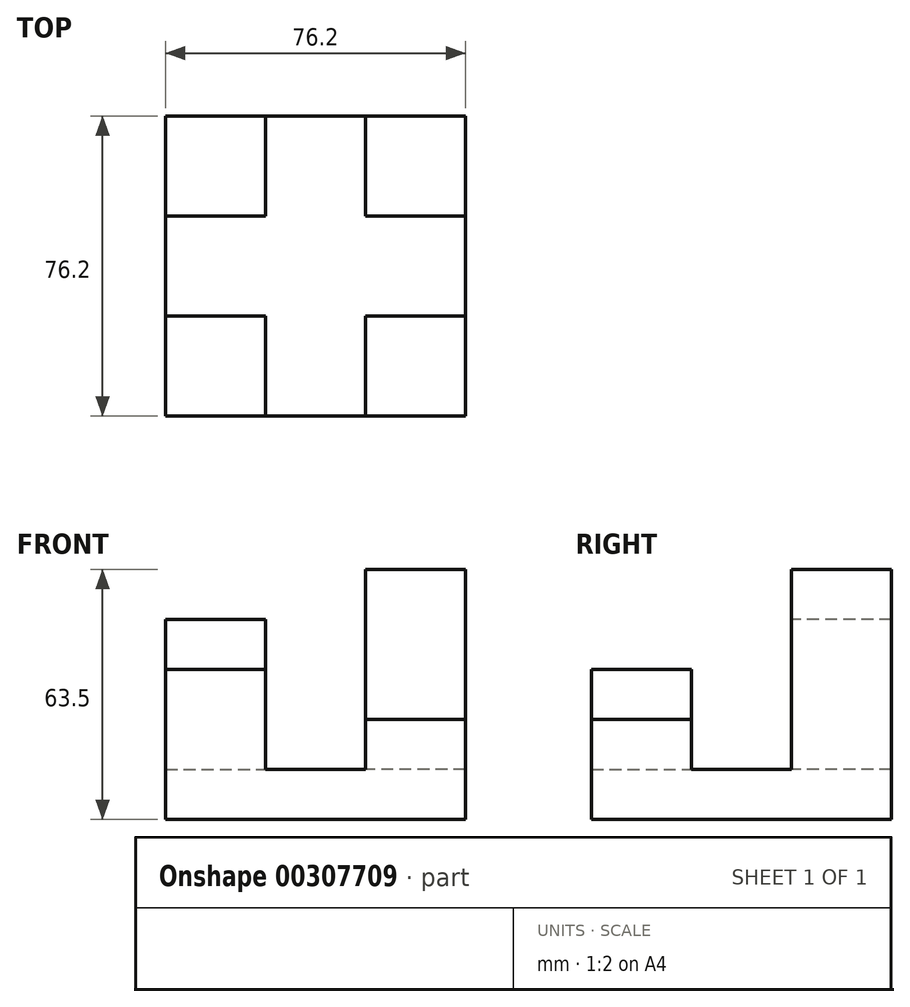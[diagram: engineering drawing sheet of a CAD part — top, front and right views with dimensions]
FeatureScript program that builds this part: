
annotation { "Feature Type Name" : "Feature", "Feature Type Description" : "" }
export const myFeature = defineFeature(function(context is Context, id is Id, definition is map)
    precondition{}
    {
        {
            var Q0;
            Q0=qCreatedBy(makeId("Top.planeOp"),FACE);
            var sketch = newSketch(context, id + "F0", { "sketchPlane" : qUnion([Q0])});
            skLineSegment(sketch, "E0.bottom", {"start": v(-34.82, 48.62) * mm, "end": v(41.38, 48.62) * mm});
            skLineSegment(sketch, "E0.top", {"start": v(-34.82, -27.58) * mm, "end": v(41.38, -27.58) * mm});
            skLineSegment(sketch, "E0.left", {"start": v(-34.82, 48.62) * mm, "end": v(-34.82, -27.58) * mm});
            skLineSegment(sketch, "E0.right", {"start": v(41.38, 48.62) * mm, "end": v(41.38, -27.58) * mm});
            skSolve(sketch);
        }
        {
            var Q0;
            Q0=makeQuery(id+"F0.imprint","IMPRINT",FACE,{"disambiguationData":[TD([[makeQuery(id+"F0.imprint","IMPRINT",EDGE,{"derivedFrom":sQuery(id+"F0.wireOp",EDGE,"E0.bottom")}),-1.0]])]});
            extrude(context, id + "F1", {"entities" : qUnion([Q0]), "depth" : 12.7 * mm});
        }
        {
            var Q0;
            Q0=makeQuery(id+"F1.opExtrude","CAP_FACE",FACE,{"disambiguationData":[OSD([sQuery(id+"F0.wireOp",EDGE,"E0.bottom"),sQuery(id+"F0.wireOp",EDGE,"E0.top"),sQuery(id+"F0.wireOp",EDGE,"E0.left"),sQuery(id+"F0.wireOp",EDGE,"E0.right")])],"isStart":false});
            var sketch = newSketch(context, id + "F2", { "sketchPlane" : qUnion([Q0])});
            skLineSegment(sketch, "E1.bottom", {"start": v(41.38, -27.58) * mm, "end": v(15.98, -27.58) * mm});
            skLineSegment(sketch, "E1.top", {"start": v(41.38, -2.18) * mm, "end": v(15.98, -2.18) * mm});
            skLineSegment(sketch, "E1.left", {"start": v(41.38, -27.58) * mm, "end": v(41.38, -2.18) * mm});
            skLineSegment(sketch, "E1.right", {"start": v(15.98, -27.58) * mm, "end": v(15.98, -2.18) * mm});
            skLineSegment(sketch, "E2.bottom", {"start": v(-34.82, -27.58) * mm, "end": v(-9.42, -27.58) * mm});
            skLineSegment(sketch, "E2.top", {"start": v(-34.82, -2.18) * mm, "end": v(-9.42, -2.18) * mm});
            skLineSegment(sketch, "E2.left", {"start": v(-34.82, -27.58) * mm, "end": v(-34.82, -2.18) * mm});
            skLineSegment(sketch, "E2.right", {"start": v(-9.42, -27.58) * mm, "end": v(-9.42, -2.18) * mm});
            skLineSegment(sketch, "E3.bottom", {"start": v(-34.82, 48.62) * mm, "end": v(-9.42, 48.62) * mm});
            skLineSegment(sketch, "E3.top", {"start": v(-34.82, 23.22) * mm, "end": v(-9.42, 23.22) * mm});
            skLineSegment(sketch, "E3.left", {"start": v(-34.82, 48.62) * mm, "end": v(-34.82, 23.22) * mm});
            skLineSegment(sketch, "E3.right", {"start": v(-9.42, 48.62) * mm, "end": v(-9.42, 23.22) * mm});
            skLineSegment(sketch, "E4.bottom", {"start": v(15.98, 48.62) * mm, "end": v(41.38, 48.62) * mm});
            skLineSegment(sketch, "E4.top", {"start": v(15.98, 23.22) * mm, "end": v(41.38, 23.22) * mm});
            skLineSegment(sketch, "E4.left", {"start": v(15.98, 48.62) * mm, "end": v(15.98, 23.22) * mm});
            skLineSegment(sketch, "E4.right", {"start": v(41.38, 48.62) * mm, "end": v(41.38, 23.22) * mm});
            skSolve(sketch);
        }
        {
            var Q0;
            Q0=makeQuery(id+"F2.imprint","IMPRINT",FACE,{"disambiguationData":[TD([[makeQuery(id+"F2.imprint","IMPRINT",EDGE,{"derivedFrom":sQuery(id+"F2.wireOp",EDGE,"E2.bottom")}),1.0]])]});
            extrude(context, id + "F3", {"entities" : qUnion([Q0]), "operationType" : NewBodyOperationType.ADD, "depth" : 25.4 * mm});
        }
        {
            var Q0;
            Q0=makeQuery(id+"F2.imprint","IMPRINT",FACE,{"disambiguationData":[TD([[makeQuery(id+"F2.imprint","IMPRINT",EDGE,{"derivedFrom":sQuery(id+"F2.wireOp",EDGE,"E1.bottom")}),1.0]])]});
            extrude(context, id + "F4", {"entities" : qUnion([Q0]), "operationType" : NewBodyOperationType.ADD, "depth" : 12.7 * mm});
        }
        {
            var Q0;
            Q0=makeQuery(id+"F2.imprint","IMPRINT",FACE,{"disambiguationData":[TD([[makeQuery(id+"F2.imprint","IMPRINT",EDGE,{"derivedFrom":sQuery(id+"F2.wireOp",EDGE,"E4.bottom")}),-1.0]])]});
            extrude(context, id + "F5", {"entities" : qUnion([Q0]), "operationType" : NewBodyOperationType.ADD, "depth" : 50.8 * mm});
        }
        {
            var Q0;
            Q0=makeQuery(id+"F2.imprint","IMPRINT",FACE,{"disambiguationData":[TD([[makeQuery(id+"F2.imprint","IMPRINT",EDGE,{"derivedFrom":sQuery(id+"F2.wireOp",EDGE,"E3.bottom")}),-1.0]])]});
            extrude(context, id + "F6", {"entities" : qUnion([Q0]), "operationType" : NewBodyOperationType.ADD, "depth" : 38.1 * mm});
        }
    });
